# Revit family: Haworth_Pip_Table_EU_PRELIMINARY
name_source: partatom
category: Furniture
revit_build: Autodesk Revit 2018 (Build: 20170223_1515(x64)
units: mm (PartAtom-declared; Revit-internal decimal feet)

## family parameters
Always vertical = Yes
Cut with Voids When Loaded = No
OmniClass Number = 23.40.20.00
OmniClass Title = General Furniture and Specialties
Room Calculation Point = No
Shared = No
Work Plane-Based = No

## types (2) — shared parameters
Actual Depth = 33 cm
Actual Height = 66 cm
Actual Width = 54 cm
Assembly Code = E2020200
Description = Haworth - Pip Table - Low
Glide Finish = Haworth _ Polymer _ Black
Manufacturer = Haworth
Model = LGTAB01
Size = Verify Final Dim. w/ Haworth
URL = https://www.haworth.com
URL - Product = https://www.haworth.com
Version = 1
Warranty = http://www.haworth.com

## per-type parameters (varying)
| type | Metal Top | Wood Top |
| Wood Top | No | Yes |
| Metal Top | Yes | No |

## geometry (parser evidence)
native form markers: Sweep x2
no freeform markers — native parametric forms only
